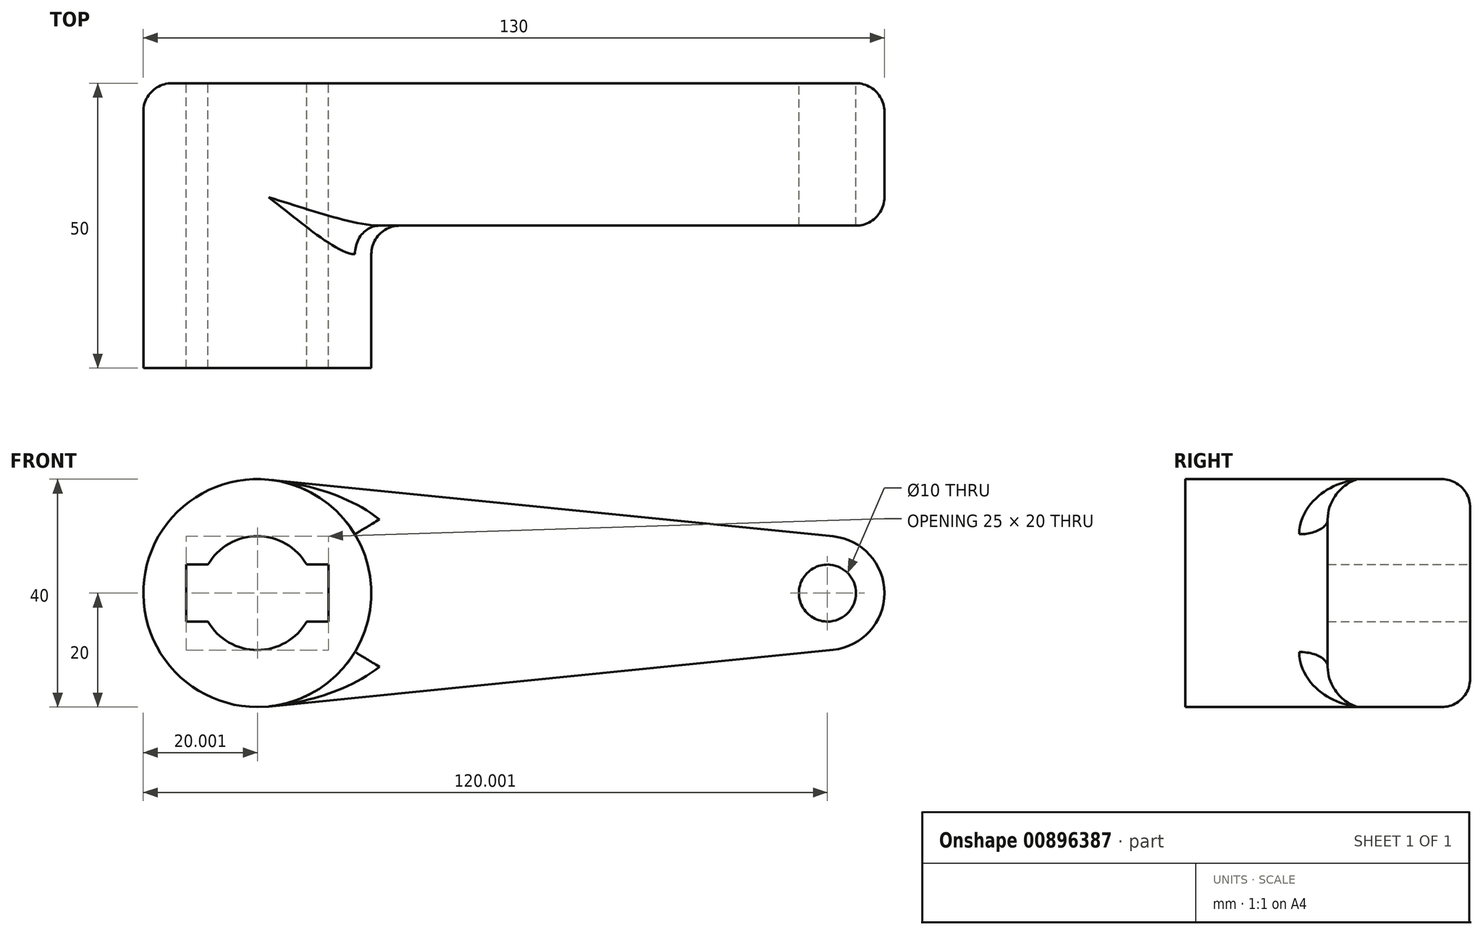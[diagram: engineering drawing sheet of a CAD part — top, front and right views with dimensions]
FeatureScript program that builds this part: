
annotation { "Feature Type Name" : "Feature", "Feature Type Description" : "" }
export const myFeature = defineFeature(function(context is Context, id is Id, definition is map)
    precondition{}
    {
        {
            var Q0;
            Q0=qCreatedBy(makeId("Front.planeOp"),FACE);
            var sketch = newSketch(context, id + "F0", { "sketchPlane" : qUnion([Q0])});
            skCircle(sketch, "E0", {"center": v(-47.4, 0) * mm, "radius": 20 * mm});
            skCircle(sketch, "E1", {"center": v(52.6, 0) * mm, "radius": 10 * mm});
            skLineSegment(sketch, "E2", {"start": v(-45.4, 19.9) * mm, "end": v(53.6, 9.95) * mm});
            skLineSegment(sketch, "E3", {"start": v(-45.4, -19.9) * mm, "end": v(53.6, -9.95) * mm});
            skCircle(sketch, "E4", {"center": v(-47.4, 0) * mm, "radius": 10 * mm});
            skCircle(sketch, "E5", {"center": v(52.6, 0) * mm, "radius": 5 * mm});
            skLineSegment(sketch, "E6.bottom", {"start": v(-59.9, 5) * mm, "end": v(-34.9, 5) * mm});
            skLineSegment(sketch, "E6.top", {"start": v(-59.9, -5) * mm, "end": v(-34.9, -5) * mm});
            skLineSegment(sketch, "E6.left", {"start": v(-59.9, 5) * mm, "end": v(-59.9, -5) * mm});
            skLineSegment(sketch, "E6.right", {"start": v(-34.9, 5) * mm, "end": v(-34.9, -5) * mm});
            skSolve(sketch);
        }
        {
            var Q0;
            {var subQ7=sQuery(id+"F0.wireOp",EDGE,"E6.left");Q0=makeQuery(id+"F0.imprint","IMPRINT",FACE,{"disambiguationData":[TD([[makeQuery(id+"F0.imprint","IMPRINT",EDGE,{"derivedFrom":subQ7}),-1.0]])]});}
            var Q1;
            {var subQ0=sQuery(id+"F0.wireOp",EDGE,"E2");Q1=makeQuery(id+"F0.imprint","IMPRINT",FACE,{"disambiguationData":[TD([[makeQuery(id+"F0.imprint","IMPRINT",EDGE,{"derivedFrom":subQ0}),-1.0]])]});}
            var Q2;
            Q2=makeQuery(id+"F0.imprint","IMPRINT",FACE,{"disambiguationData":[TD([[makeQuery(id+"F0.imprint","IMPRINT",EDGE,{"derivedFrom":sQuery(id+"F0.wireOp",EDGE,"E5")}),-1.0]])]});
            extrude(context, id + "F1", {"entities" : qUnion([Q0, Q1, Q2]), "depth" : 25 * mm, "offsetDistance" : 25 * mm});
        }
        {
            var Q0;
            {var subQ7=sQuery(id+"F0.wireOp",EDGE,"E6.left");Q0=makeQuery(id+"F0.imprint","IMPRINT",FACE,{"disambiguationData":[TD([[makeQuery(id+"F0.imprint","IMPRINT",EDGE,{"derivedFrom":subQ7}),-1.0]])]});}
            extrude(context, id + "F2", {"entities" : qUnion([Q0]), "operationType" : NewBodyOperationType.ADD, "depth" : 50 * mm, "offsetDistance" : 25 * mm});
        }
        {
            var Q0;
            {var subQ0=sQuery(id+"F0.wireOp",EDGE,"E0");Q0=makeQuery(id+"F2.boolean.opBoolean","INTERSECT",EDGE,{"derivedFrom":[makeQuery(id+"F1.opExtrude","CAP_FACE",FACE,{"disambiguationData":[OSD([subQ0,sQuery(id+"F0.wireOp",EDGE,"E1"),sQuery(id+"F0.wireOp",EDGE,"E2"),sQuery(id+"F0.wireOp",EDGE,"E3"),sQuery(id+"F0.wireOp",EDGE,"E4"),sQuery(id+"F0.wireOp",EDGE,"E5"),sQuery(id+"F0.wireOp",EDGE,"E6.bottom"),sQuery(id+"F0.wireOp",EDGE,"E6.top"),sQuery(id+"F0.wireOp",EDGE,"E6.left"),sQuery(id+"F0.wireOp",EDGE,"E6.right")])],"isStart":false}),makeQuery(id+"F2.opExtrude","SWEPT_FACE",FACE,{"disambiguationData":[OSD([subQ0])]})]});}
            var Q1;
            Q1=makeQuery(id+"F1.opExtrude","CAP_EDGE",EDGE,{"disambiguationData":[OSD([sQuery(id+"F0.wireOp",EDGE,"E3")])],"isStart":false});
            var Q2;
            Q2=makeQuery(id+"F1.opExtrude","CAP_EDGE",EDGE,{"disambiguationData":[OSD([sQuery(id+"F0.wireOp",EDGE,"E1")])],"isStart":false});
            var Q3;
            Q3=makeQuery(id+"F1.opExtrude","CAP_EDGE",EDGE,{"disambiguationData":[OSD([sQuery(id+"F0.wireOp",EDGE,"E2")])],"isStart":false});
            var Q4;
            Q4=makeQuery(id+"F1.opExtrude","CAP_EDGE",EDGE,{"disambiguationData":[OSD([sQuery(id+"F0.wireOp",EDGE,"E3")])],"isStart":true});
            var Q5;
            Q5=makeQuery(id+"F1.opExtrude","CAP_EDGE",EDGE,{"disambiguationData":[OSD([sQuery(id+"F0.wireOp",EDGE,"E1")])],"isStart":true});
            var Q6;
            Q6=makeQuery(id+"F1.opExtrude","CAP_EDGE",EDGE,{"disambiguationData":[OSD([sQuery(id+"F0.wireOp",EDGE,"E2")])],"isStart":true});
            var Q7;
            Q7=makeQuery(id+"F1.opExtrude","CAP_EDGE",EDGE,{"disambiguationData":[OSD([sQuery(id+"F0.wireOp",EDGE,"E0")])],"isStart":true});
            fillet(context, id + "F3", {"entities" : qUnion([Q0, Q1, Q2, Q3, Q4, Q5, Q6, Q7]), "radius" : 5 * mm, "tangentPropagation" : true, "allowEdgeOverflow" : false});
        }
    });
